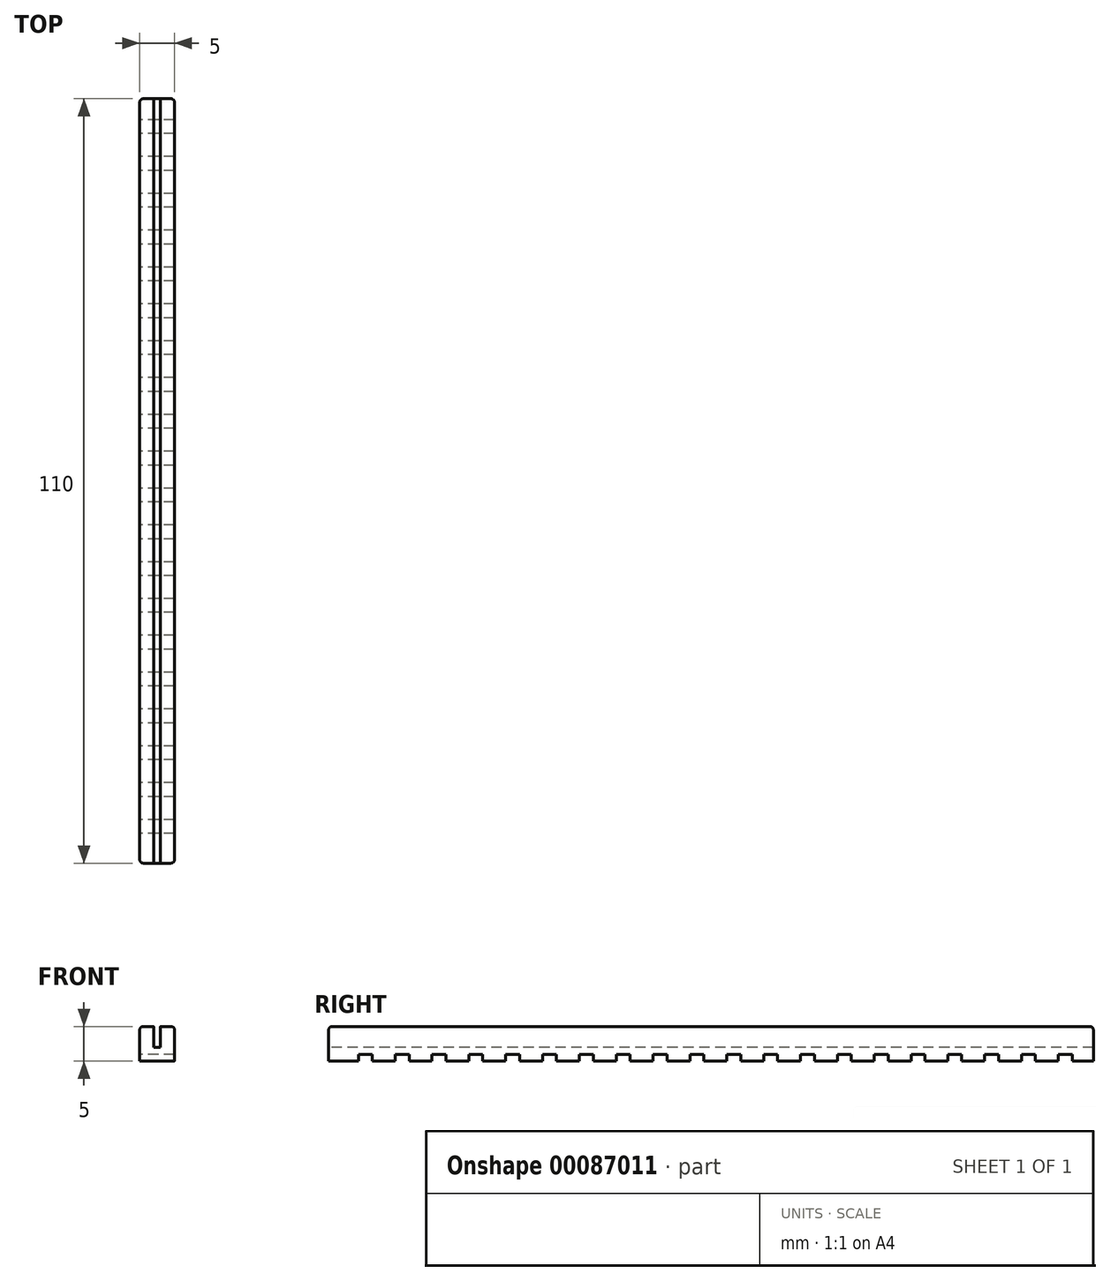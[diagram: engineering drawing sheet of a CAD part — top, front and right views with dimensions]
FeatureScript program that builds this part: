
annotation { "Feature Type Name" : "Feature", "Feature Type Description" : "" }
export const myFeature = defineFeature(function(context is Context, id is Id, definition is map)
    precondition{}
    {
        {
            var Q0;
            Q0=qCreatedBy(makeId("Top.planeOp"),FACE);
            var sketch = newSketch(context, id + "F0", { "sketchPlane" : qUnion([Q0])});
            skLineSegment(sketch, "E0.bottom", {"start": v(-2.5, 54.48) * mm, "end": v(-0.5, 54.48) * mm});
            skLineSegment(sketch, "E0.top", {"start": v(-2.5, -55.52) * mm, "end": v(-0.5, -55.52) * mm});
            skLineSegment(sketch, "E0.left", {"start": v(-2.5, 54.48) * mm, "end": v(-2.5, -55.52) * mm});
            skLineSegment(sketch, "E0.right", {"start": v(-0.5, 54.48) * mm, "end": v(-0.5, -55.52) * mm});
            skLineSegment(sketch, "E1.bottom", {"start": v(-0.5, 54.48) * mm, "end": v(0, 54.48) * mm});
            skLineSegment(sketch, "E1.top", {"start": v(-0.5, -55.52) * mm, "end": v(0, -55.52) * mm});
            skLineSegment(sketch, "E1.right", {"start": v(0, 54.48) * mm, "end": v(0, -55.52) * mm});
            skLineSegment(sketch, "E2", {"start": v(0, 68.43) * mm, "end": v(0, -62.55) * mm, "construction": true});
            skLineSegment(sketch, "E3.MirrorCS", {"start": v(0.5, 54.48) * mm, "end": v(0, 54.48) * mm});
            skLineSegment(sketch, "E4.MirrorCS", {"start": v(0.5, 54.48) * mm, "end": v(0.5, -55.52) * mm});
            skLineSegment(sketch, "E5.MirrorCS", {"start": v(2.5, 54.48) * mm, "end": v(0.5, 54.48) * mm});
            skLineSegment(sketch, "E6.MirrorCS", {"start": v(2.5, 54.48) * mm, "end": v(2.5, -55.52) * mm});
            skLineSegment(sketch, "E7.MirrorCS", {"start": v(2.5, -55.52) * mm, "end": v(0.5, -55.52) * mm});
            skLineSegment(sketch, "E8.MirrorCS", {"start": v(0.5, -55.52) * mm, "end": v(0, -55.52) * mm});
            skSolve(sketch);
        }
        {
            var Q0;
            Q0=makeQuery(id+"F0.imprint","IMPRINT",FACE,{"disambiguationData":[TD([[makeQuery(id+"F0.imprint","IMPRINT",EDGE,{"derivedFrom":sQuery(id+"F0.wireOp",EDGE,"E1.bottom")}),-1.0]])]});
            var Q1;
            Q1=makeQuery(id+"F0.imprint","IMPRINT",FACE,{"disambiguationData":[TD([[makeQuery(id+"F0.imprint","IMPRINT",EDGE,{"derivedFrom":sQuery(id+"F0.wireOp",EDGE,"E1.right")}),1.0]])]});
            extrude(context, id + "F1", {"entities" : qUnion([Q0, Q1]), "depth" : 2 * mm});
        }
        {
            var Q0;
            Q0=makeQuery(id+"F0.imprint","IMPRINT",FACE,{"disambiguationData":[TD([[makeQuery(id+"F0.imprint","IMPRINT",EDGE,{"derivedFrom":sQuery(id+"F0.wireOp",EDGE,"E0.bottom")}),-1.0]])]});
            var Q1;
            Q1=makeQuery(id+"F0.imprint","IMPRINT",FACE,{"disambiguationData":[TD([[makeQuery(id+"F0.imprint","IMPRINT",EDGE,{"derivedFrom":sQuery(id+"F0.wireOp",EDGE,"E4.MirrorCS")}),1.0]])]});
            extrude(context, id + "F2", {"entities" : qUnion([Q0, Q1]), "operationType" : NewBodyOperationType.ADD, "depth" : 5 * mm});
        }
        {
            var Q0;
            Q0=makeQuery(id+"F2.opExtrude","SWEPT_EDGE",EDGE,{"disambiguationData":[OSD([sQuery(id+"F0.wireOp",EDGE,"E0.top"),sQuery(id+"F0.wireOp",EDGE,"E0.left")])]});
            var Q1;
            Q1=makeQuery(id+"F2.opExtrude","CAP_EDGE",EDGE,{"disambiguationData":[OSD([sQuery(id+"F0.wireOp",EDGE,"E0.top")])],"isStart":false});
            var Q2;
            Q2=makeQuery(id+"F2.opExtrude","CAP_EDGE",EDGE,{"disambiguationData":[OSD([sQuery(id+"F0.wireOp",EDGE,"E7.MirrorCS")])],"isStart":false});
            var Q3;
            Q3=makeQuery(id+"F2.opExtrude","SWEPT_EDGE",EDGE,{"disambiguationData":[OSD([sQuery(id+"F0.wireOp",EDGE,"E6.MirrorCS"),sQuery(id+"F0.wireOp",EDGE,"E7.MirrorCS")])]});
            var Q4;
            Q4=makeQuery(id+"F2.opExtrude","CAP_EDGE",EDGE,{"disambiguationData":[OSD([sQuery(id+"F0.wireOp",EDGE,"E6.MirrorCS")])],"isStart":false});
            var Q5;
            Q5=makeQuery(id+"F2.opExtrude","CAP_EDGE",EDGE,{"disambiguationData":[OSD([sQuery(id+"F0.wireOp",EDGE,"E0.left")])],"isStart":false});
            var Q6;
            Q6=makeQuery(id+"F2.opExtrude","CAP_EDGE",EDGE,{"disambiguationData":[OSD([sQuery(id+"F0.wireOp",EDGE,"E0.bottom")])],"isStart":false});
            var Q7;
            Q7=makeQuery(id+"F2.opExtrude","CAP_EDGE",EDGE,{"disambiguationData":[OSD([sQuery(id+"F0.wireOp",EDGE,"E5.MirrorCS")])],"isStart":false});
            var Q8;
            Q8=makeQuery(id+"F2.opExtrude","SWEPT_EDGE",EDGE,{"disambiguationData":[OSD([sQuery(id+"F0.wireOp",EDGE,"E5.MirrorCS"),sQuery(id+"F0.wireOp",EDGE,"E6.MirrorCS")])]});
            var Q9;
            Q9=makeQuery(id+"F2.opExtrude","SWEPT_EDGE",EDGE,{"disambiguationData":[OSD([sQuery(id+"F0.wireOp",EDGE,"E0.bottom"),sQuery(id+"F0.wireOp",EDGE,"E0.left")])]});
            fillet(context, id + "F3", {"entities" : qUnion([Q0, Q1, Q2, Q3, Q4, Q5, Q6, Q7, Q8, Q9]), "radius" : .5 * mm, "tangentPropagation" : true, "allowEdgeOverflow" : false});
        }
        {
            var Q0;
            Q0=makeQuery(id+"F2.opExtrude","SWEPT_FACE",FACE,{"disambiguationData":[OSD([sQuery(id+"F0.wireOp",EDGE,"E0.left")])]});
            var sketch = newSketch(context, id + "F4", { "sketchPlane" : qUnion([Q0])});
            skLineSegment(sketch, "E9.bottom", {"start": v(-51.45, 0) * mm, "end": v(-49.45, 0) * mm});
            skLineSegment(sketch, "E9.top", {"start": v(-51.45, 1) * mm, "end": v(-49.45, 1) * mm});
            skLineSegment(sketch, "E9.left", {"start": v(-51.45, 0) * mm, "end": v(-51.45, 1) * mm});
            skLineSegment(sketch, "E9.right", {"start": v(-49.45, 0) * mm, "end": v(-49.45, 1) * mm});
            skLineSegment(sketch, "E10.1.0.0", {"start": v(-46.15, 0) * mm, "end": v(-44.15, 0) * mm});
            skLineSegment(sketch, "E10.1.0.1", {"start": v(-46.15, 0) * mm, "end": v(-46.15, 1) * mm});
            skLineSegment(sketch, "E10.1.0.2", {"start": v(-46.15, 1) * mm, "end": v(-44.15, 1) * mm});
            skLineSegment(sketch, "E10.1.0.3", {"start": v(-44.15, 0) * mm, "end": v(-44.15, 1) * mm});
            skLineSegment(sketch, "E10.2.0.0", {"start": v(-40.85, 0) * mm, "end": v(-38.85, 0) * mm});
            skLineSegment(sketch, "E10.2.0.1", {"start": v(-40.85, 0) * mm, "end": v(-40.85, 1) * mm});
            skLineSegment(sketch, "E10.2.0.2", {"start": v(-40.85, 1) * mm, "end": v(-38.85, 1) * mm});
            skLineSegment(sketch, "E10.2.0.3", {"start": v(-38.85, 0) * mm, "end": v(-38.85, 1) * mm});
            skLineSegment(sketch, "E10.3.0.0", {"start": v(-35.55, 0) * mm, "end": v(-33.55, 0) * mm});
            skLineSegment(sketch, "E10.3.0.1", {"start": v(-35.55, 0) * mm, "end": v(-35.55, 1) * mm});
            skLineSegment(sketch, "E10.3.0.2", {"start": v(-35.55, 1) * mm, "end": v(-33.55, 1) * mm});
            skLineSegment(sketch, "E10.3.0.3", {"start": v(-33.55, 0) * mm, "end": v(-33.55, 1) * mm});
            skLineSegment(sketch, "E10.4.0.0", {"start": v(-30.25, 0) * mm, "end": v(-28.25, 0) * mm});
            skLineSegment(sketch, "E10.4.0.1", {"start": v(-30.25, 0) * mm, "end": v(-30.25, 1) * mm});
            skLineSegment(sketch, "E10.4.0.2", {"start": v(-30.25, 1) * mm, "end": v(-28.25, 1) * mm});
            skLineSegment(sketch, "E10.4.0.3", {"start": v(-28.25, 0) * mm, "end": v(-28.25, 1) * mm});
            skLineSegment(sketch, "E10.5.0.0", {"start": v(-24.95, 0) * mm, "end": v(-22.95, 0) * mm});
            skLineSegment(sketch, "E10.5.0.1", {"start": v(-24.95, 0) * mm, "end": v(-24.95, 1) * mm});
            skLineSegment(sketch, "E10.5.0.2", {"start": v(-24.95, 1) * mm, "end": v(-22.95, 1) * mm});
            skLineSegment(sketch, "E10.5.0.3", {"start": v(-22.95, 0) * mm, "end": v(-22.95, 1) * mm});
            skLineSegment(sketch, "E10.6.0.0", {"start": v(-19.65, 0) * mm, "end": v(-17.65, 0) * mm});
            skLineSegment(sketch, "E10.6.0.1", {"start": v(-19.65, 0) * mm, "end": v(-19.65, 1) * mm});
            skLineSegment(sketch, "E10.6.0.2", {"start": v(-19.65, 1) * mm, "end": v(-17.65, 1) * mm});
            skLineSegment(sketch, "E10.6.0.3", {"start": v(-17.65, 0) * mm, "end": v(-17.65, 1) * mm});
            skLineSegment(sketch, "E10.7.0.0", {"start": v(-14.35, 0) * mm, "end": v(-12.35, 0) * mm});
            skLineSegment(sketch, "E10.7.0.1", {"start": v(-14.35, 0) * mm, "end": v(-14.35, 1) * mm});
            skLineSegment(sketch, "E10.7.0.2", {"start": v(-14.35, 1) * mm, "end": v(-12.35, 1) * mm});
            skLineSegment(sketch, "E10.7.0.3", {"start": v(-12.35, 0) * mm, "end": v(-12.35, 1) * mm});
            skLineSegment(sketch, "E10.8.0.0", {"start": v(-9.05, 0) * mm, "end": v(-7.05, 0) * mm});
            skLineSegment(sketch, "E10.8.0.1", {"start": v(-9.05, 0) * mm, "end": v(-9.05, 1) * mm});
            skLineSegment(sketch, "E10.8.0.2", {"start": v(-9.05, 1) * mm, "end": v(-7.05, 1) * mm});
            skLineSegment(sketch, "E10.8.0.3", {"start": v(-7.05, 0) * mm, "end": v(-7.05, 1) * mm});
            skLineSegment(sketch, "E10.9.0.0", {"start": v(-3.75, 0) * mm, "end": v(-1.75, 0) * mm});
            skLineSegment(sketch, "E10.9.0.1", {"start": v(-3.75, 0) * mm, "end": v(-3.75, 1) * mm});
            skLineSegment(sketch, "E10.9.0.2", {"start": v(-3.75, 1) * mm, "end": v(-1.75, 1) * mm});
            skLineSegment(sketch, "E10.9.0.3", {"start": v(-1.75, 0) * mm, "end": v(-1.75, 1) * mm});
            skLineSegment(sketch, "E10.10.0.0", {"start": v(1.55, 0) * mm, "end": v(3.55, 0) * mm});
            skLineSegment(sketch, "E10.10.0.1", {"start": v(1.55, 0) * mm, "end": v(1.55, 1) * mm});
            skLineSegment(sketch, "E10.10.0.2", {"start": v(1.55, 1) * mm, "end": v(3.55, 1) * mm});
            skLineSegment(sketch, "E10.10.0.3", {"start": v(3.55, 0) * mm, "end": v(3.55, 1) * mm});
            skLineSegment(sketch, "E10.11.0.0", {"start": v(6.85, 0) * mm, "end": v(8.85, 0) * mm});
            skLineSegment(sketch, "E10.11.0.1", {"start": v(6.85, 0) * mm, "end": v(6.85, 1) * mm});
            skLineSegment(sketch, "E10.11.0.2", {"start": v(6.85, 1) * mm, "end": v(8.85, 1) * mm});
            skLineSegment(sketch, "E10.11.0.3", {"start": v(8.85, 0) * mm, "end": v(8.85, 1) * mm});
            skLineSegment(sketch, "E10.12.0.0", {"start": v(12.15, 0) * mm, "end": v(14.15, 0) * mm});
            skLineSegment(sketch, "E10.12.0.1", {"start": v(12.15, 0) * mm, "end": v(12.15, 1) * mm});
            skLineSegment(sketch, "E10.12.0.2", {"start": v(12.15, 1) * mm, "end": v(14.15, 1) * mm});
            skLineSegment(sketch, "E10.12.0.3", {"start": v(14.15, 0) * mm, "end": v(14.15, 1) * mm});
            skLineSegment(sketch, "E10.13.0.0", {"start": v(17.45, 0) * mm, "end": v(19.45, 0) * mm});
            skLineSegment(sketch, "E10.13.0.1", {"start": v(17.45, 0) * mm, "end": v(17.45, 1) * mm});
            skLineSegment(sketch, "E10.13.0.2", {"start": v(17.45, 1) * mm, "end": v(19.45, 1) * mm});
            skLineSegment(sketch, "E10.13.0.3", {"start": v(19.45, 0) * mm, "end": v(19.45, 1) * mm});
            skLineSegment(sketch, "E10.14.0.0", {"start": v(22.75, 0) * mm, "end": v(24.75, 0) * mm});
            skLineSegment(sketch, "E10.14.0.1", {"start": v(22.75, 0) * mm, "end": v(22.75, 1) * mm});
            skLineSegment(sketch, "E10.14.0.2", {"start": v(22.75, 1) * mm, "end": v(24.75, 1) * mm});
            skLineSegment(sketch, "E10.14.0.3", {"start": v(24.75, 0) * mm, "end": v(24.75, 1) * mm});
            skLineSegment(sketch, "E10.15.0.0", {"start": v(28.05, 0) * mm, "end": v(30.05, 0) * mm});
            skLineSegment(sketch, "E10.15.0.1", {"start": v(28.05, 0) * mm, "end": v(28.05, 1) * mm});
            skLineSegment(sketch, "E10.15.0.2", {"start": v(28.05, 1) * mm, "end": v(30.05, 1) * mm});
            skLineSegment(sketch, "E10.15.0.3", {"start": v(30.05, 0) * mm, "end": v(30.05, 1) * mm});
            skLineSegment(sketch, "E10.16.0.0", {"start": v(33.35, 0) * mm, "end": v(35.35, 0) * mm});
            skLineSegment(sketch, "E10.16.0.1", {"start": v(33.35, 0) * mm, "end": v(33.35, 1) * mm});
            skLineSegment(sketch, "E10.16.0.2", {"start": v(33.35, 1) * mm, "end": v(35.35, 1) * mm});
            skLineSegment(sketch, "E10.16.0.3", {"start": v(35.35, 0) * mm, "end": v(35.35, 1) * mm});
            skLineSegment(sketch, "E10.17.0.0", {"start": v(38.65, 0) * mm, "end": v(40.65, 0) * mm});
            skLineSegment(sketch, "E10.17.0.1", {"start": v(38.65, 0) * mm, "end": v(38.65, 1) * mm});
            skLineSegment(sketch, "E10.17.0.2", {"start": v(38.65, 1) * mm, "end": v(40.65, 1) * mm});
            skLineSegment(sketch, "E10.17.0.3", {"start": v(40.65, 0) * mm, "end": v(40.65, 1) * mm});
            skLineSegment(sketch, "E10.18.0.0", {"start": v(43.95, 0) * mm, "end": v(45.95, 0) * mm});
            skLineSegment(sketch, "E10.18.0.1", {"start": v(43.95, 0) * mm, "end": v(43.95, 1) * mm});
            skLineSegment(sketch, "E10.18.0.2", {"start": v(43.95, 1) * mm, "end": v(45.95, 1) * mm});
            skLineSegment(sketch, "E10.18.0.3", {"start": v(45.95, 0) * mm, "end": v(45.95, 1) * mm});
            skLineSegment(sketch, "E10.19.0.0", {"start": v(49.25, 0) * mm, "end": v(51.25, 0) * mm});
            skLineSegment(sketch, "E10.19.0.1", {"start": v(49.25, 0) * mm, "end": v(49.25, 1) * mm});
            skLineSegment(sketch, "E10.19.0.2", {"start": v(49.25, 1) * mm, "end": v(51.25, 1) * mm});
            skLineSegment(sketch, "E10.19.0.3", {"start": v(51.25, 0) * mm, "end": v(51.25, 1) * mm});
            skLineSegment(sketch, "E10.direction1", {"start": v(-51.45, 0) * mm, "end": v(-46.15, 0) * mm, "construction": true});
            skSolve(sketch);
        }
        {
            var Q0;
            Q0 = qSketchRegion(id + "F4", true);
            extrude(context, id + "F5", {"entities" : qUnion([Q0]), "operationType" : NewBodyOperationType.REMOVE, "oppositeDirection" : true, "depth" : 28.68 * mm});
        }
    });
